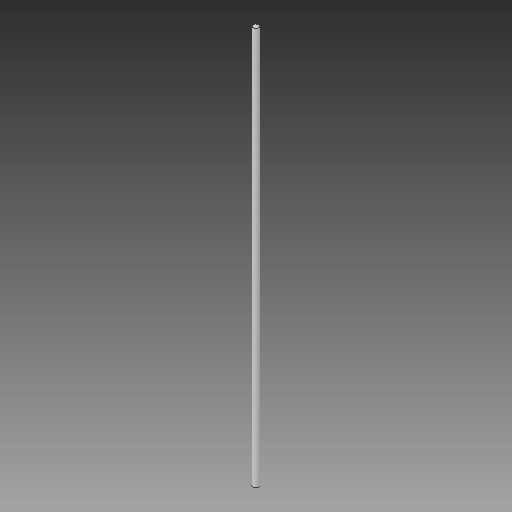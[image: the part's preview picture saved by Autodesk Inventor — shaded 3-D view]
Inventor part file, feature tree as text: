
AUTODESK INVENTOR PART (.ipt)
format: ipt  version: 2017 (Build 210142000, 142)  size: 71,168 bytes
history: native  units: mm
features: other x3, sketch x1
ambient origin geometry x8: Origin, YZ Plane, XZ Plane, XY Plane, X Axis, Y Axis, Z Axis, Center Point
bodies: Solid1 (feature_tree)
feature tree (4):
  other  "12mmSmoothRod_CPY.ipt"
  other  "Solid1::12mmSmoothRod_CPY.ipt"
  other  "TaggingFeature1"
  sketch  "Sketch1"  dims[d0=10.0mm]
